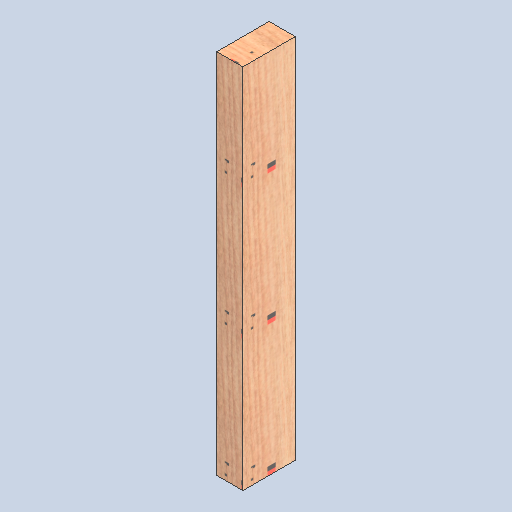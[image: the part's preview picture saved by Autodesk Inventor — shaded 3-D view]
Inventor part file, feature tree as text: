
AUTODESK INVENTOR PART (.ipt)
format: ipt  version: 2025 (Build 290162000, 162)  size: 168,960 bytes
history: native  units: in
note: dims shown in document units (in); Inventor stores cm internally (conversion verified against a paired STEP export)
features: extrude x1, sketch x1
ambient origin geometry x8: Origin, YZ Plane, XZ Plane, XY Plane, X Axis, Y Axis, Z Axis, Center Point
bodies: Solid1 (feature_tree)
feature tree (2):
  extrude  "Extrusion1"  Depth=4.0in
  sketch  "Sketch1"  dims[d0=2.0in d1=4.0in d2=28.0in d3=0.0in]
